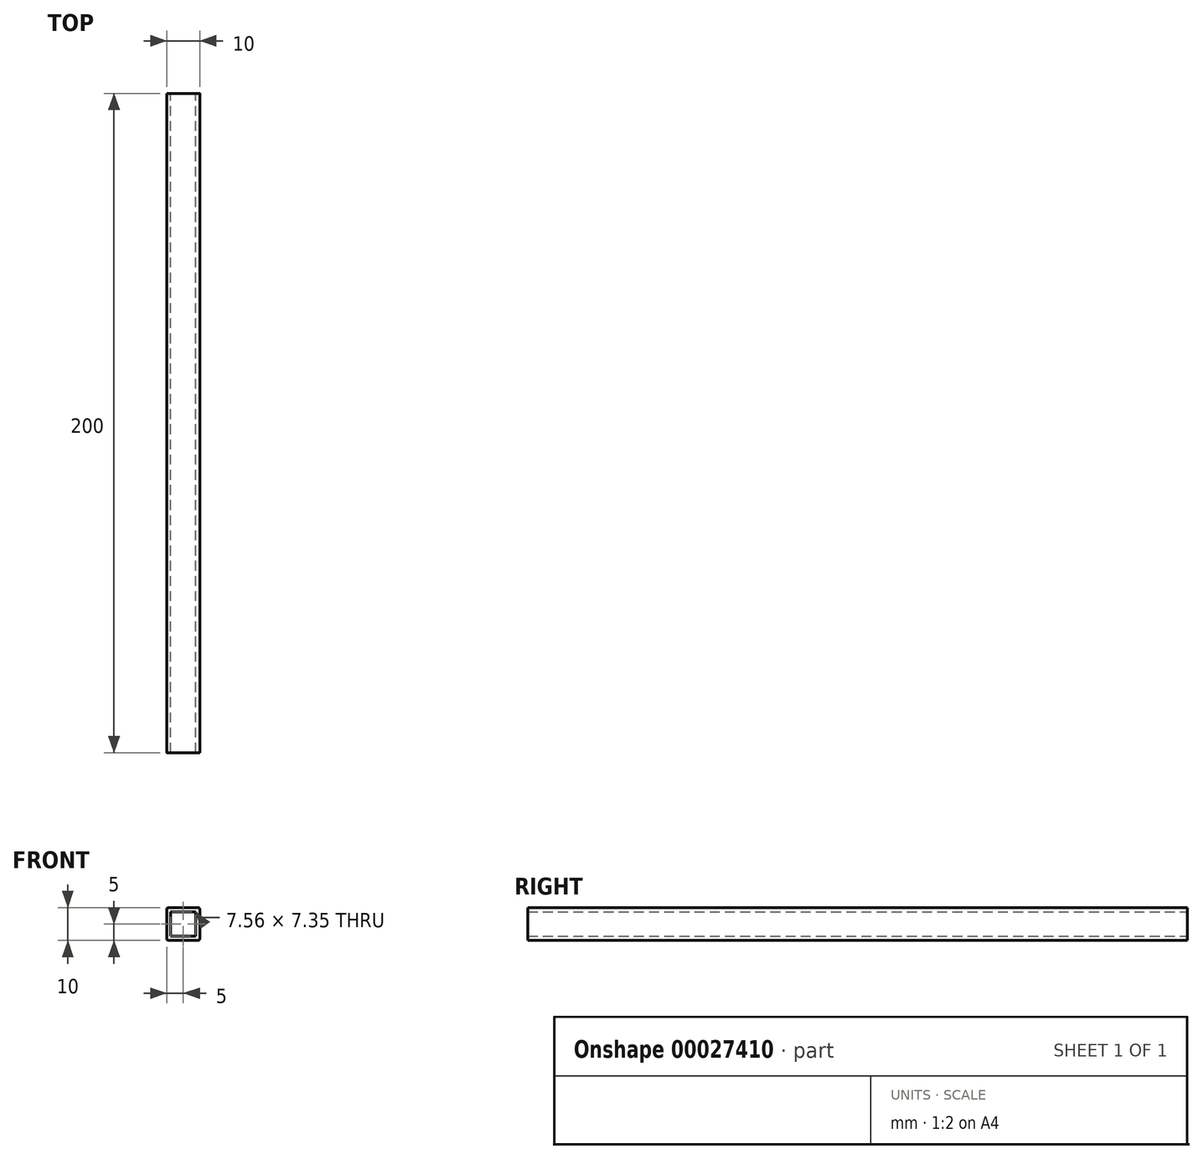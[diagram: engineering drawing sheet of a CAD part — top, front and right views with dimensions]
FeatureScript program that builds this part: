
annotation { "Feature Type Name" : "Feature", "Feature Type Description" : "" }
export const myFeature = defineFeature(function(context is Context, id is Id, definition is map)
    precondition{}
    {
        {
            var Q0;
            Q0=qCreatedBy(makeId("Front.planeOp"),FACE);
            var sketch = newSketch(context, id + "F0", { "sketchPlane" : qUnion([Q0])});
            skLineSegment(sketch, "E0.rect.bottom", {"start": v(4.5, -5) * mm, "end": v(-4.5, -5) * mm});
            skLineSegment(sketch, "E0.rect.top", {"start": v(4.5, 5) * mm, "end": v(-4.5, 5) * mm});
            skLineSegment(sketch, "E0.rect.left", {"start": v(5, -4.5) * mm, "end": v(5, 4.5) * mm});
            skLineSegment(sketch, "E0.rect.right", {"start": v(-5, -4.5) * mm, "end": v(-5, 4.5) * mm});
            skPoint(sketch, "E0.rect.middle", {"position": v(0, 0) * mm});
            skPoint(sketch, "E1.visualSharp", {"position": v(-5, 5) * mm});
            skArc(sketch, "E1.filletArc", {"start": v(-4.5, 5) * mm, "mid": v(-4.85, 4.85) * mm, "end": v(-5, 4.5) * mm});
            skPoint(sketch, "E2.visualSharp", {"position": v(5, 5) * mm});
            skArc(sketch, "E2.filletArc", {"start": v(5, 4.5) * mm, "mid": v(4.85, 4.85) * mm, "end": v(4.5, 5) * mm});
            skPoint(sketch, "E3.visualSharp", {"position": v(5, -5) * mm});
            skArc(sketch, "E3.filletArc", {"start": v(4.5, -5) * mm, "mid": v(4.85, -4.85) * mm, "end": v(5, -4.5) * mm});
            skPoint(sketch, "E4.visualSharp", {"position": v(-5, -5) * mm});
            skArc(sketch, "E4.filletArc", {"start": v(-5, -4.5) * mm, "mid": v(-4.85, -4.85) * mm, "end": v(-4.5, -5) * mm});
            skLineSegment(sketch, "E5.rect.bottom", {"start": v(3.78, -3.67) * mm, "end": v(-3.78, -3.67) * mm});
            skLineSegment(sketch, "E5.rect.top", {"start": v(3.78, 3.67) * mm, "end": v(-3.78, 3.67) * mm});
            skLineSegment(sketch, "E5.rect.left", {"start": v(3.78, -3.67) * mm, "end": v(3.78, 3.67) * mm});
            skLineSegment(sketch, "E5.rect.right", {"start": v(-3.78, -3.67) * mm, "end": v(-3.78, 3.67) * mm});
            skSolve(sketch);
        }
        {
            var Q0;
            Q0=makeQuery(id+"F0.imprint","IMPRINT",FACE,{"disambiguationData":[TD([[makeQuery(id+"F0.imprint","IMPRINT",EDGE,{"derivedFrom":sQuery(id+"F0.wireOp",EDGE,"E0.rect.bottom")}),-1.0]])]});
            extrude(context, id + "F1", {"entities" : qUnion([Q0]), "depth" : 150 * mm, "hasSecondDirection" : true, "secondDirectionOppositeDirection" : true, "secondDirectionDepth" : 50 * mm});
        }
    });
